# Revit family: Bathtub-Integral_Apron-DXV-Byrdcliffe-D02390202
name_source: partatom
category: Plumbing Fixtures
units: mm (PartAtom-declared; Revit-internal decimal feet)

## family parameters
Always vertical = No
Cut with Voids When Loaded = No
OmniClass Number = 23.45.05.14.21
OmniClass Title = Bathtubs
Part Type = Normal
Room Calculation Point = No
Round Connector Dimension = Use Radius
Shared = Yes
Work Plane-Based = Yes

## types (1)
- D02390202.415
    Assembly Code = D2010510
    CW Connection = No
    CWFU = 3
    Default Elevation = 0"
    Description = Classically designed and perfect for traditional bathroom decor, the Byrdcliffe Recessed Tub adds luxury to your bathroom.The bathtub features an integral apron and is ideal for alcove tub installations.
    Finish = Porcelain-DXV-415-Canvas White
    HW Connection = No
    HWFU = 3
    Height = 14"
    IAPMO Compliance = Meets or Exceeds ASME A112.19.1/CSA B45.2/ ASTM F462
    Installation Type = Floor Mounted
    Length = 60"
    Manufacturer = DXV
    Material = Porcelain-DXV-415-Canvas White
    Model = D02390202.415
    Price = Prices may vary. Please consult Manufacturer Representative for most up-to-date price list.
    Product Documentation Link = https://dxv01.blob.core.windows.net
    Product Page URL = https://www.dxv.com
    Revised Date = 01/19/2022
    URL = http://www.dxv.com
    Vent Connection = No
    WFU = 4
    Warranty Information = Lifetime Limited Warranty
    Waste Connection = Yes
    Waste Connection Diameter = 1 1/2"
    Waste Connection Radius = 3/4"
    Waste Connection Width = 7 3/4"
    Width = 30"

## geometry (parser evidence)
native form markers: Sweep x2
no freeform markers — native parametric forms only
